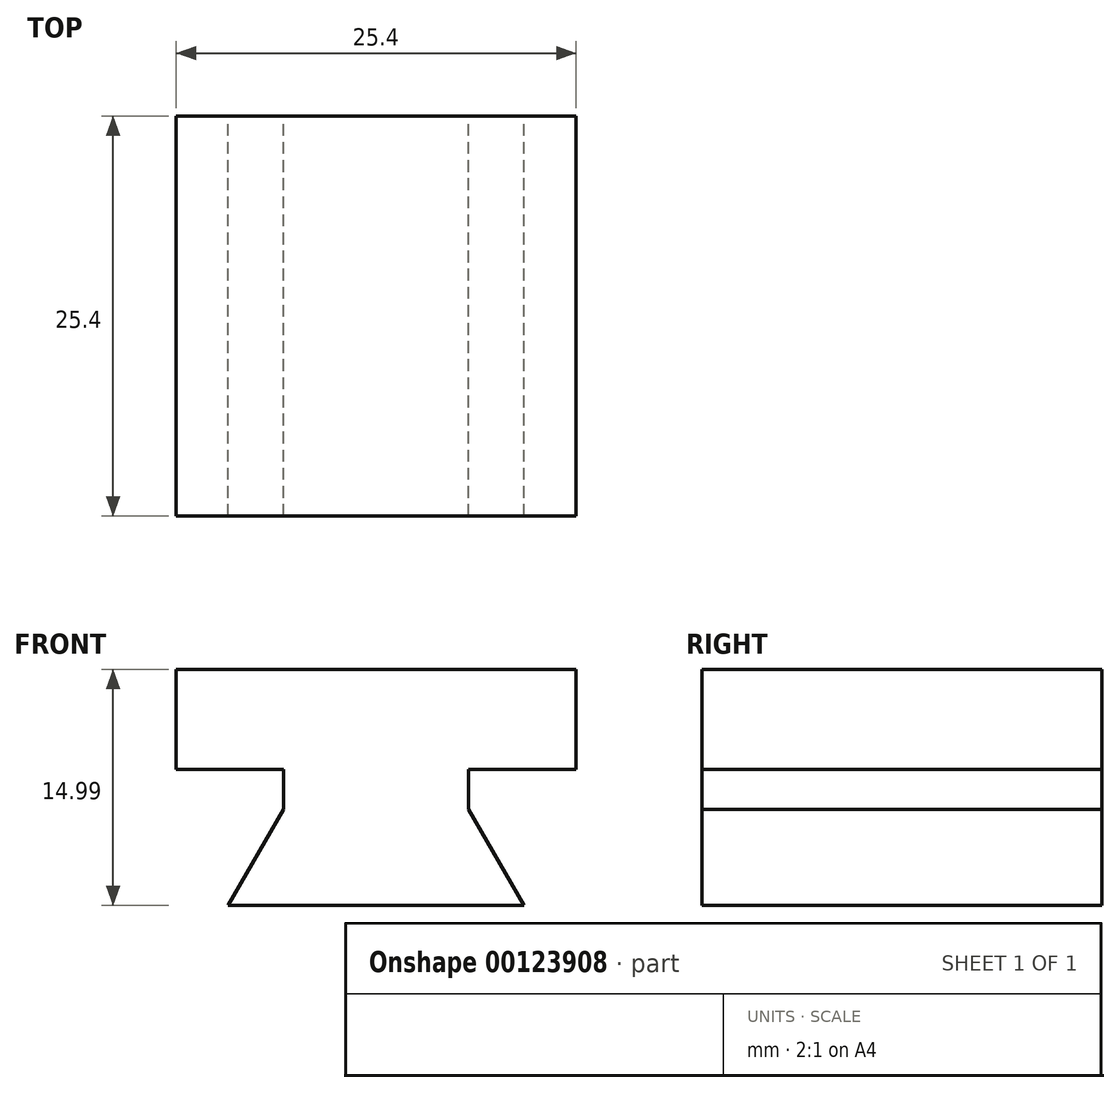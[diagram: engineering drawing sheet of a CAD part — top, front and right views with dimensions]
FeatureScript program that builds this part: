
annotation { "Feature Type Name" : "Feature", "Feature Type Description" : "" }
export const myFeature = defineFeature(function(context is Context, id is Id, definition is map)
    precondition{}
    {
        {
            var Q0;
            Q0=qCreatedBy(makeId("Front.planeOp"),FACE);
            var sketch = newSketch(context, id + "F0", { "sketchPlane" : qUnion([Q0])});
            skLineSegment(sketch, "E0", {"start": v(-9.4, 0) * mm, "end": v(9.4, 0) * mm});
            skLineSegment(sketch, "E1", {"start": v(9.4, 0) * mm, "end": v(5.88, 6.1) * mm});
            skLineSegment(sketch, "E2", {"start": v(5.88, 6.1) * mm, "end": v(-5.88, 6.1) * mm});
            skLineSegment(sketch, "E3", {"start": v(-5.88, 6.1) * mm, "end": v(-9.4, 0) * mm});
            skLineSegment(sketch, "E4", {"start": v(0, 0) * mm, "end": v(0, 6.1) * mm, "construction": true});
            skSolve(sketch);
        }
        {
            var Q0;
            Q0 = qSketchRegion(id + "F0", true);
            extrude(context, id + "F1", {"entities" : qUnion([Q0]), "depth" : 12.7 * mm, "hasSecondDirection" : true, "secondDirectionOppositeDirection" : true, "secondDirectionDepth" : 12.7 * mm});
        }
        {
            var Q0;
            Q0=makeQuery(id+"F1.opExtrude","SWEPT_FACE",FACE,{"disambiguationData":[OSD([sQuery(id+"F0.wireOp",EDGE,"E2")])]});
            var sketch = newSketch(context, id + "F2", { "sketchPlane" : qUnion([Q0])});
            skLineSegment(sketch, "E5.bottom", {"start": v(-5.88, 12.7) * mm, "end": v(5.88, 12.7) * mm});
            skLineSegment(sketch, "E5.top", {"start": v(-5.88, -12.7) * mm, "end": v(5.88, -12.7) * mm});
            skLineSegment(sketch, "E5.left", {"start": v(-5.88, 12.7) * mm, "end": v(-5.88, -12.7) * mm});
            skLineSegment(sketch, "E5.right", {"start": v(5.88, 12.7) * mm, "end": v(5.88, -12.7) * mm});
            skSolve(sketch);
        }
        {
            var Q0;
            Q0 = qSketchRegion(id + "F2", true);
            extrude(context, id + "F3", {"entities" : qUnion([Q0]), "operationType" : NewBodyOperationType.ADD, "depth" : 2.54 * mm});
        }
        {
            var Q0;
            Q0=makeQuery(id+"F3.opExtrude","CAP_FACE",FACE,{"disambiguationData":[OSD([sQuery(id+"F2.wireOp",EDGE,"E5.bottom"),sQuery(id+"F2.wireOp",EDGE,"E5.top"),sQuery(id+"F2.wireOp",EDGE,"E5.left"),sQuery(id+"F2.wireOp",EDGE,"E5.right")])],"isStart":false});
            var sketch = newSketch(context, id + "F4", { "sketchPlane" : qUnion([Q0])});
            skLineSegment(sketch, "E6.bottom", {"start": v(-12.7, 12.7) * mm, "end": v(12.7, 12.7) * mm});
            skLineSegment(sketch, "E6.top", {"start": v(-12.7, -12.7) * mm, "end": v(12.7, -12.7) * mm});
            skLineSegment(sketch, "E6.left", {"start": v(-12.7, 12.7) * mm, "end": v(-12.7, -12.7) * mm});
            skLineSegment(sketch, "E7", {"start": v(-12.7, 0) * mm, "end": v(0, 0) * mm, "construction": true});
            skLineSegment(sketch, "E8", {"start": v(12.7, 12.7) * mm, "end": v(12.7, -12.7) * mm});
            skLineSegment(sketch, "E9", {"start": v(0, 0) * mm, "end": v(12.7, 0) * mm, "construction": true});
            skSolve(sketch);
        }
        {
            var Q0;
            Q0 = qSketchRegion(id + "F4", true);
            extrude(context, id + "F5", {"entities" : qUnion([Q0]), "operationType" : NewBodyOperationType.ADD, "depth" : 6.35 * mm});
        }
    });
